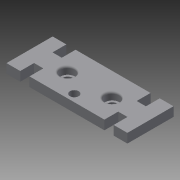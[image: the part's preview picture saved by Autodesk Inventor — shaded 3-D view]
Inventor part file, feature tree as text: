
AUTODESK INVENTOR PART (.ipt)
format: ipt  version: 2015 (Build 190159000, 159)  size: 139,264 bytes
history: native  units: mm
features: extrude x4, sketch x3, fillet x1
ambient origin geometry x8: Origin, YZ Plane, XZ Plane, XY Plane, X Axis, Y Axis, Z Axis, Center Point
bodies: Body1 (feature_tree)
feature tree (8):
  sketch  "Sketch1"  dims[d0=15.0mm d1=15.0mm d2=15.0mm d3=15.0mm d8=15.0mm]
  extrude  "Extrusion2"  Depth=15.0mm
  extrude  "Extrusion3"  Depth=10.0mm TaperAngle=0.0deg
  sketch  "Sketch3"  dims[d15=2.5mm d16=2.5mm d17=10.0mm d18=0.0mm d25=48.2mm d35=8.0mm d36=9.5mm d37=10.0mm d38=0.0mm d39=10.0mm d40=10.0mm d41=2.0mm d42=0.0mm d43=2.0mm]
  extrude  "Extrusion8"  Depth=2.0mm
  extrude  "Extrusion9"  Depth=10.0mm TaperAngle=0.0deg
  fillet  "Fillet1"  Radius=48.2mm
  sketch  "Sketch2"  dims[d9=15.0mm d10=10.0mm d11=0.0mm]
